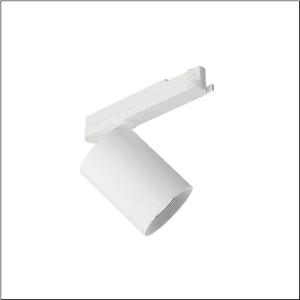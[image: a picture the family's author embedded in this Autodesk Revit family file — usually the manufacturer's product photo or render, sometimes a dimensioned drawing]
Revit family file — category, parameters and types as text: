
# Revit family: spot_21_51se13mba5b
name_source: partatom
category: Lighting Fixtures
units: mm (PartAtom-declared; Revit-internal decimal feet)

## family parameters
Cut with Voids When Loaded = No
Host = Face
Light Source = No
Part Type = Normal
Room Calculation Point = No
Round Connector Dimension = Use Diameter
Shared = No

## types (1)
- --- (1 x LED, 5300 lm, 41.8 W, 2700K)
    Apparent Load = 42 VA
    CIE Flux Codes = 95 98 99 100 100
    Color Rendering = 90
    Color Temperature = 2700K
    Default Elevation = 1800 mm
    Description = Spot 21, directional spotlight, light control with lens, of PMMA, LED rated luminous flux: 5.090lm, light colour: 927, control gear: ECG Multilumen, with 3-phase adapter, mains connection: 220..240V, AC, 50/60Hz, of aluminium, traffic white (RAL 9016), length: 213mm, diameter: 105mm, protection rating (complete): IP20, insulation class (complete): insulation class I (protective earthing), certification: CE, impact resistance: IK02, permissible ambient temperature for indoor applications: -20..+40°C, packaging unit: 1 piece
    Height = 175 mm
    Lamp = 1 x LED
    Lamp Light Flux = 5300 lm
    Lamp Power = 41.8 W
    Lamp count = 1
    Length = 105 mm
    Luminous efficacy = 127 lm/W
    Manufacturer = Siteco
    ModVariant = No
    Model = 51SE13MBA5B
    Mounting Place = Ceiling
    Mounting Type = Pendant
    Number of Poles = 1
    OnlyDefault = Yes
    Power Factor = 1
    Product Name = Spot 21
    Product group = directional spotlight
    ProductGroupID = 905
    Protection Class = Protection class I
    Protection Degree = IP 20
    RLX_Detail_Level = 1
    RLX_Emergency_Light_Flux = 0 lm
    RLX_Emergency_Type = 0
    RLX_Emergency_Type_DB = No
    RlxData = <blob elided: 17617 chars, md5=22601275>
    Socket = socket
    Standby Power = 0 W
    System Light Flux = 5300 lm
    System Power = 42 W
    Type Comments = factory setting: luminous flux: 100 % | (ON | ON | ON | ON) | 1050 mA
    Type Image = l_1003976.jpg
    URL = http://relux.com
    VarID = @adj_075765
    Voltage = 0 V
    Weight = 0.00 kg
    Width = 0 mm  [stored 0 ft]

note: [stored X ft] marks values corroborated as IEEE doubles in the binary element streams (Revit-internal decimal feet)

## geometry (parser evidence)
native form markers: Blend x4, Sweep x10
no freeform markers — native parametric forms only
